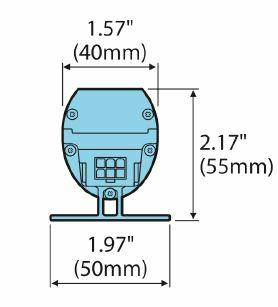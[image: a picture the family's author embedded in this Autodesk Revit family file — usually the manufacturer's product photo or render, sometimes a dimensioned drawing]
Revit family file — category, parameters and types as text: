
# Revit family: Lighting-Linear-Acclaim-Adapt-Linear-2.0
name_source: partatom
category: Lighting Fixtures
revit_build: Autodesk Revit 2017 (Build: 20190508_0315(x64)
units: mm (PartAtom-declared; Revit-internal decimal feet)

## family parameters
Cut with Voids When Loaded = No
Host = Face
Light Source = Yes
Part Type = Normal
Room Calculation Point = No
Round Connector Dimension = Use Diameter
Shared = No

## types (1)
- Lighting-Linear-Acclaim-Adapt-Linear-2.0
    Apparent Load = 0 VA
    Color Filter = 16777215
    Default Elevation = 48 "
    Description = Linear LED
    Dimming Lamp Color Temperature Shift = <None>
    Emit from Line Length = 24 "
    Height = 2.17 "
    Housing Finish = Aluminum
    Lamp = LED
    Length = 24 "
    Manufacturer = Acclaim Lighting
    Model = Adapt Linear 2.0
    Number of Poles = 1
    Photometric Web File = Load File
    Power Factor = 1
    Tilt Angle = -90.00°
    URL = http://www.acclaimlighting.com
    Voltage = 0 V
    Width = 2.57 "

## geometry (parser evidence)
native form markers: Blend x13, Sweep x2
no freeform markers — native parametric forms only
